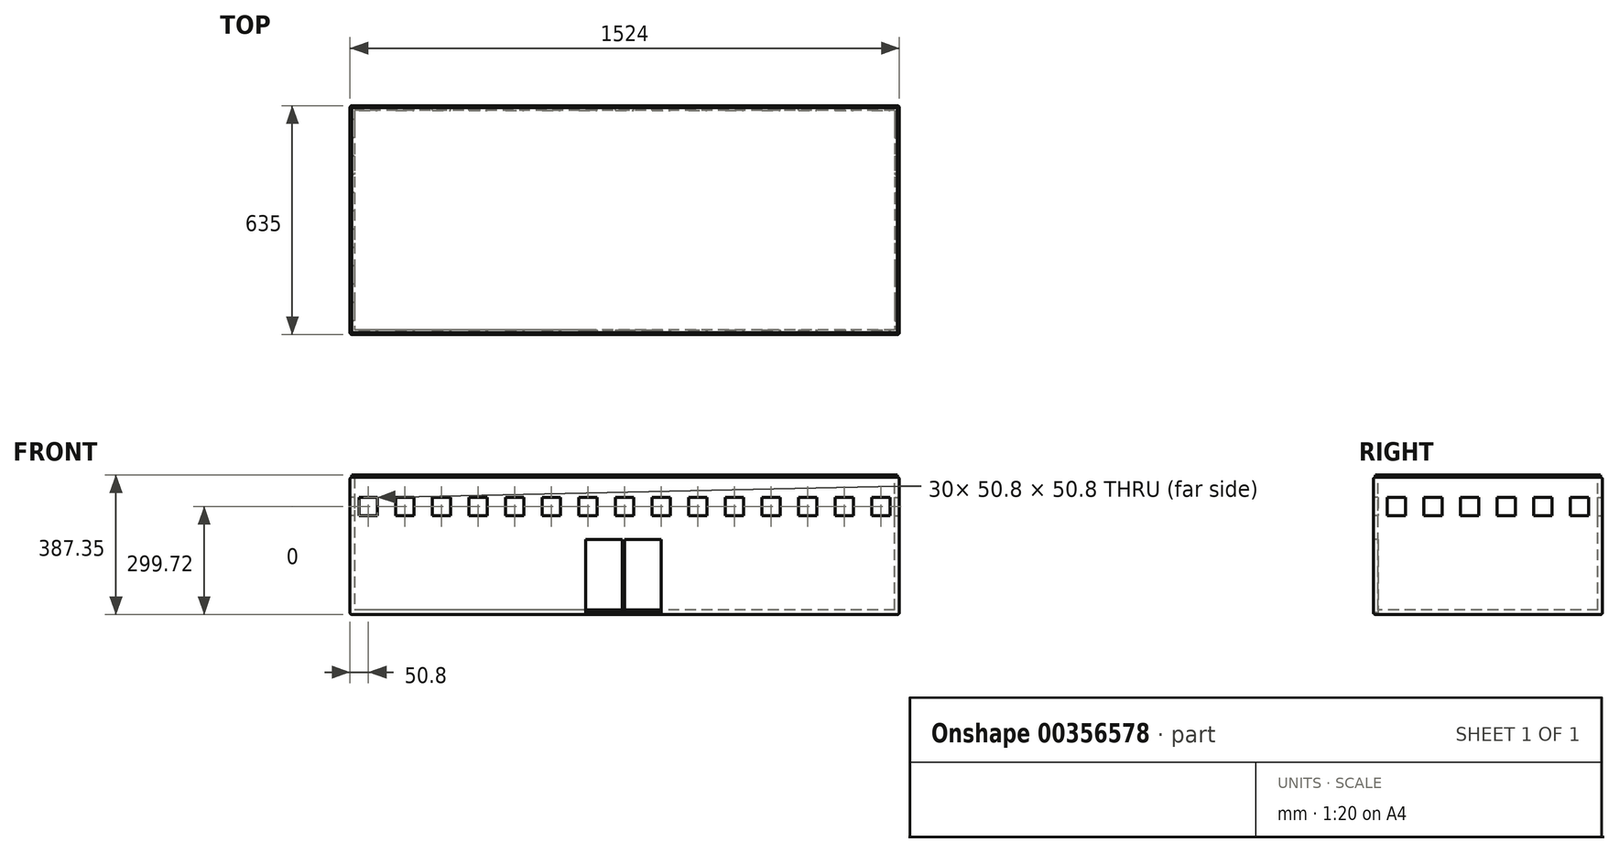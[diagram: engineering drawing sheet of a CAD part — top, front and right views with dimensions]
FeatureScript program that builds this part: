
annotation { "Feature Type Name" : "Feature", "Feature Type Description" : "" }
export const myFeature = defineFeature(function(context is Context, id is Id, definition is map)
    precondition{}
    {
        {
            var Q0;
            Q0=qCreatedBy(makeId("Top.planeOp"),FACE);
            var sketch = newSketch(context, id + "F0", { "sketchPlane" : qUnion([Q0])});
            skLineSegment(sketch, "E0.bottom", {"start": v(-762, 317.5) * mm, "end": v(762, 317.5) * mm});
            skLineSegment(sketch, "E0.top", {"start": v(-762, -317.5) * mm, "end": v(762, -317.5) * mm});
            skLineSegment(sketch, "E0.left", {"start": v(-762, 317.5) * mm, "end": v(-762, -317.5) * mm});
            skLineSegment(sketch, "E0.right", {"start": v(762, 317.5) * mm, "end": v(762, -317.5) * mm});
            skPoint(sketch, "E0.middle", {"position": v(0, 0) * mm});
            skSolve(sketch);
        }
        {
            var Q0;
            Q0 = qSketchRegion(id + "F0", true);
            extrude(context, id + "F1", {"entities" : qUnion([Q0]), "depth" : 381 * mm});
        }
        {
            var Q0;
            Q0=makeQuery(id+"F1.opExtrude","CAP_FACE",FACE,{"disambiguationData":[OSD([sQuery(id+"F0.wireOp",EDGE,"E0.bottom"),sQuery(id+"F0.wireOp",EDGE,"E0.top"),sQuery(id+"F0.wireOp",EDGE,"E0.left"),sQuery(id+"F0.wireOp",EDGE,"E0.right")])],"isStart":false});
            var Q1;
            Q1=makeQuery(id+"F1.opExtrude","SWEPT_FACE",FACE,{"disambiguationData":[OSD([sQuery(id+"F0.wireOp",EDGE,"E0.top")])]});
            var Q2;
            Q2=makeQuery(id+"F1.opExtrude","CAP_FACE",FACE,{"disambiguationData":[OSD([sQuery(id+"F0.wireOp",EDGE,"E0.bottom"),sQuery(id+"F0.wireOp",EDGE,"E0.top"),sQuery(id+"F0.wireOp",EDGE,"E0.left"),sQuery(id+"F0.wireOp",EDGE,"E0.right")])],"isStart":true});
            var Q3;
            Q3=makeQuery(id+"F1.opExtrude","SWEPT_FACE",FACE,{"disambiguationData":[OSD([sQuery(id+"F0.wireOp",EDGE,"E0.bottom")])]});
            fillet(context, id + "F2", {"entities" : qUnion([Q0, Q1, Q2, Q3]), "radius" : 5.08 * mm, "tangentPropagation" : true, "allowEdgeOverflow" : false});
        }
        {
            var Q0;
            Q0=makeQuery(id+"F1.opExtrude","CAP_FACE",FACE,{"disambiguationData":[OSD([sQuery(id+"F0.wireOp",EDGE,"E0.bottom"),sQuery(id+"F0.wireOp",EDGE,"E0.top"),sQuery(id+"F0.wireOp",EDGE,"E0.left"),sQuery(id+"F0.wireOp",EDGE,"E0.right")])],"isStart":false});
            shell(context, id + "F3", {"entities" : qUnion([Q0]), "thickness" : 12.7 * mm});
        }
        {
            var Q0;
            Q0=makeQuery(id+"F1.opExtrude","SWEPT_FACE",FACE,{"disambiguationData":[OSD([sQuery(id+"F0.wireOp",EDGE,"E0.top")])]});
            var sketch = newSketch(context, id + "F4", { "sketchPlane" : qUnion([Q0])});
            skLineSegment(sketch, "E1.bottom", {"start": v(-107.95, 208.28) * mm, "end": v(-6.35, 208.28) * mm});
            skLineSegment(sketch, "E1.top", {"start": v(-107.95, 5.08) * mm, "end": v(-6.35, 5.08) * mm});
            skLineSegment(sketch, "E1.left", {"start": v(-107.95, 208.28) * mm, "end": v(-107.95, 5.08) * mm});
            skLineSegment(sketch, "E1.right", {"start": v(-6.35, 208.28) * mm, "end": v(-6.35, 5.08) * mm});
            skLineSegment(sketch, "E2.bottom", {"start": v(0, 208.28) * mm, "end": v(101.6, 208.28) * mm});
            skLineSegment(sketch, "E2.top", {"start": v(0, 5.08) * mm, "end": v(101.6, 5.08) * mm});
            skLineSegment(sketch, "E2.left", {"start": v(0, 208.28) * mm, "end": v(0, 5.08) * mm});
            skLineSegment(sketch, "E2.right", {"start": v(101.6, 208.28) * mm, "end": v(101.6, 5.08) * mm});
            skSolve(sketch);
        }
        {
            var Q0;
            Q0 = qSketchRegion(id + "F4", true);
            extrude(context, id + "F5", {"entities" : qUnion([Q0]), "operationType" : NewBodyOperationType.REMOVE, "oppositeDirection" : true, "depth" : 12.7 * mm});
        }
        {
            var Q0;
            Q0=makeQuery(id+"F1.opExtrude","SWEPT_FACE",FACE,{"disambiguationData":[OSD([sQuery(id+"F0.wireOp",EDGE,"E0.top")])]});
            var sketch = newSketch(context, id + "F6", { "sketchPlane" : qUnion([Q0])});
            skLineSegment(sketch, "E3.bottom", {"start": v(-685.8, 274.32) * mm, "end": v(-736.6, 274.32) * mm});
            skLineSegment(sketch, "E3.top", {"start": v(-685.8, 325.12) * mm, "end": v(-736.6, 325.12) * mm});
            skLineSegment(sketch, "E3.left", {"start": v(-685.8, 274.32) * mm, "end": v(-685.8, 325.12) * mm});
            skLineSegment(sketch, "E3.right", {"start": v(-736.6, 274.32) * mm, "end": v(-736.6, 325.12) * mm});
            skPoint(sketch, "E3.middle", {"position": v(-711.2, 299.72) * mm});
            skLineSegment(sketch, "E4.1.0.0", {"start": v(-584.2, 274.32) * mm, "end": v(-635, 274.32) * mm});
            skLineSegment(sketch, "E4.1.0.1", {"start": v(-584.2, 325.12) * mm, "end": v(-635, 325.12) * mm});
            skLineSegment(sketch, "E4.1.0.2", {"start": v(-584.2, 274.32) * mm, "end": v(-584.2, 325.12) * mm});
            skLineSegment(sketch, "E4.1.0.3", {"start": v(-635, 274.32) * mm, "end": v(-635, 325.12) * mm});
            skPoint(sketch, "E4.1.0.4", {"position": v(-609.6, 299.72) * mm});
            skLineSegment(sketch, "E4.2.0.0", {"start": v(-482.6, 274.32) * mm, "end": v(-533.4, 274.32) * mm});
            skLineSegment(sketch, "E4.2.0.1", {"start": v(-482.6, 325.12) * mm, "end": v(-533.4, 325.12) * mm});
            skLineSegment(sketch, "E4.2.0.2", {"start": v(-482.6, 274.32) * mm, "end": v(-482.6, 325.12) * mm});
            skLineSegment(sketch, "E4.2.0.3", {"start": v(-533.4, 274.32) * mm, "end": v(-533.4, 325.12) * mm});
            skPoint(sketch, "E4.2.0.4", {"position": v(-508, 299.72) * mm});
            skLineSegment(sketch, "E4.3.0.0", {"start": v(-381, 274.32) * mm, "end": v(-431.8, 274.32) * mm});
            skLineSegment(sketch, "E4.3.0.1", {"start": v(-381, 325.12) * mm, "end": v(-431.8, 325.12) * mm});
            skLineSegment(sketch, "E4.3.0.2", {"start": v(-381, 274.32) * mm, "end": v(-381, 325.12) * mm});
            skLineSegment(sketch, "E4.3.0.3", {"start": v(-431.8, 274.32) * mm, "end": v(-431.8, 325.12) * mm});
            skPoint(sketch, "E4.3.0.4", {"position": v(-406.4, 299.72) * mm});
            skLineSegment(sketch, "E4.4.0.0", {"start": v(-279.4, 274.32) * mm, "end": v(-330.2, 274.32) * mm});
            skLineSegment(sketch, "E4.4.0.1", {"start": v(-279.4, 325.12) * mm, "end": v(-330.2, 325.12) * mm});
            skLineSegment(sketch, "E4.4.0.2", {"start": v(-279.4, 274.32) * mm, "end": v(-279.4, 325.12) * mm});
            skLineSegment(sketch, "E4.4.0.3", {"start": v(-330.2, 274.32) * mm, "end": v(-330.2, 325.12) * mm});
            skPoint(sketch, "E4.4.0.4", {"position": v(-304.8, 299.72) * mm});
            skLineSegment(sketch, "E4.5.0.0", {"start": v(-177.8, 274.32) * mm, "end": v(-228.6, 274.32) * mm});
            skLineSegment(sketch, "E4.5.0.1", {"start": v(-177.8, 325.12) * mm, "end": v(-228.6, 325.12) * mm});
            skLineSegment(sketch, "E4.5.0.2", {"start": v(-177.8, 274.32) * mm, "end": v(-177.8, 325.12) * mm});
            skLineSegment(sketch, "E4.5.0.3", {"start": v(-228.6, 274.32) * mm, "end": v(-228.6, 325.12) * mm});
            skPoint(sketch, "E4.5.0.4", {"position": v(-203.2, 299.72) * mm});
            skLineSegment(sketch, "E4.6.0.0", {"start": v(-76.2, 274.32) * mm, "end": v(-127, 274.32) * mm});
            skLineSegment(sketch, "E4.6.0.1", {"start": v(-76.2, 325.12) * mm, "end": v(-127, 325.12) * mm});
            skLineSegment(sketch, "E4.6.0.2", {"start": v(-76.2, 274.32) * mm, "end": v(-76.2, 325.12) * mm});
            skLineSegment(sketch, "E4.6.0.3", {"start": v(-127, 274.32) * mm, "end": v(-127, 325.12) * mm});
            skPoint(sketch, "E4.6.0.4", {"position": v(-101.6, 299.72) * mm});
            skLineSegment(sketch, "E4.7.0.0", {"start": v(25.4, 274.32) * mm, "end": v(-25.4, 274.32) * mm});
            skLineSegment(sketch, "E4.7.0.1", {"start": v(25.4, 325.12) * mm, "end": v(-25.4, 325.12) * mm});
            skLineSegment(sketch, "E4.7.0.2", {"start": v(25.4, 274.32) * mm, "end": v(25.4, 325.12) * mm});
            skLineSegment(sketch, "E4.7.0.3", {"start": v(-25.4, 274.32) * mm, "end": v(-25.4, 325.12) * mm});
            skPoint(sketch, "E4.7.0.4", {"position": v(0, 299.72) * mm});
            skLineSegment(sketch, "E4.8.0.0", {"start": v(127, 274.32) * mm, "end": v(76.2, 274.32) * mm});
            skLineSegment(sketch, "E4.8.0.1", {"start": v(127, 325.12) * mm, "end": v(76.2, 325.12) * mm});
            skLineSegment(sketch, "E4.8.0.2", {"start": v(127, 274.32) * mm, "end": v(127, 325.12) * mm});
            skLineSegment(sketch, "E4.8.0.3", {"start": v(76.2, 274.32) * mm, "end": v(76.2, 325.12) * mm});
            skPoint(sketch, "E4.8.0.4", {"position": v(101.6, 299.72) * mm});
            skLineSegment(sketch, "E4.9.0.0", {"start": v(228.6, 274.32) * mm, "end": v(177.8, 274.32) * mm});
            skLineSegment(sketch, "E4.9.0.1", {"start": v(228.6, 325.12) * mm, "end": v(177.8, 325.12) * mm});
            skLineSegment(sketch, "E4.9.0.2", {"start": v(228.6, 274.32) * mm, "end": v(228.6, 325.12) * mm});
            skLineSegment(sketch, "E4.9.0.3", {"start": v(177.8, 274.32) * mm, "end": v(177.8, 325.12) * mm});
            skPoint(sketch, "E4.9.0.4", {"position": v(203.2, 299.72) * mm});
            skLineSegment(sketch, "E4.10.0.0", {"start": v(330.2, 274.32) * mm, "end": v(279.4, 274.32) * mm});
            skLineSegment(sketch, "E4.10.0.1", {"start": v(330.2, 325.12) * mm, "end": v(279.4, 325.12) * mm});
            skLineSegment(sketch, "E4.10.0.2", {"start": v(330.2, 274.32) * mm, "end": v(330.2, 325.12) * mm});
            skLineSegment(sketch, "E4.10.0.3", {"start": v(279.4, 274.32) * mm, "end": v(279.4, 325.12) * mm});
            skPoint(sketch, "E4.10.0.4", {"position": v(304.8, 299.72) * mm});
            skLineSegment(sketch, "E4.11.0.0", {"start": v(431.8, 274.32) * mm, "end": v(381, 274.32) * mm});
            skLineSegment(sketch, "E4.11.0.1", {"start": v(431.8, 325.12) * mm, "end": v(381, 325.12) * mm});
            skLineSegment(sketch, "E4.11.0.2", {"start": v(431.8, 274.32) * mm, "end": v(431.8, 325.12) * mm});
            skLineSegment(sketch, "E4.11.0.3", {"start": v(381, 274.32) * mm, "end": v(381, 325.12) * mm});
            skPoint(sketch, "E4.11.0.4", {"position": v(406.4, 299.72) * mm});
            skLineSegment(sketch, "E4.12.0.0", {"start": v(533.4, 274.32) * mm, "end": v(482.6, 274.32) * mm});
            skLineSegment(sketch, "E4.12.0.1", {"start": v(533.4, 325.12) * mm, "end": v(482.6, 325.12) * mm});
            skLineSegment(sketch, "E4.12.0.2", {"start": v(533.4, 274.32) * mm, "end": v(533.4, 325.12) * mm});
            skLineSegment(sketch, "E4.12.0.3", {"start": v(482.6, 274.32) * mm, "end": v(482.6, 325.12) * mm});
            skPoint(sketch, "E4.12.0.4", {"position": v(508, 299.72) * mm});
            skLineSegment(sketch, "E4.13.0.0", {"start": v(635, 274.32) * mm, "end": v(584.2, 274.32) * mm});
            skLineSegment(sketch, "E4.13.0.1", {"start": v(635, 325.12) * mm, "end": v(584.2, 325.12) * mm});
            skLineSegment(sketch, "E4.13.0.2", {"start": v(635, 274.32) * mm, "end": v(635, 325.12) * mm});
            skLineSegment(sketch, "E4.13.0.3", {"start": v(584.2, 274.32) * mm, "end": v(584.2, 325.12) * mm});
            skPoint(sketch, "E4.13.0.4", {"position": v(609.6, 299.72) * mm});
            skLineSegment(sketch, "E4.14.0.0", {"start": v(736.6, 274.32) * mm, "end": v(685.8, 274.32) * mm});
            skLineSegment(sketch, "E4.14.0.1", {"start": v(736.6, 325.12) * mm, "end": v(685.8, 325.12) * mm});
            skLineSegment(sketch, "E4.14.0.2", {"start": v(736.6, 274.32) * mm, "end": v(736.6, 325.12) * mm});
            skLineSegment(sketch, "E4.14.0.3", {"start": v(685.8, 274.32) * mm, "end": v(685.8, 325.12) * mm});
            skPoint(sketch, "E4.14.0.4", {"position": v(711.2, 299.72) * mm});
            skLineSegment(sketch, "E4.direction1", {"start": v(-736.6, 274.32) * mm, "end": v(-635, 274.32) * mm, "construction": true});
            skSolve(sketch);
        }
        {
            var Q0;
            Q0=makeQuery(id+"F6.imprint","IMPRINT",FACE,{"disambiguationData":[TD([[makeQuery(id+"F6.imprint","IMPRINT",EDGE,{"derivedFrom":sQuery(id+"F6.wireOp",EDGE,"E4.1.0.0")}),-1.0]])]});
            var Q1;
            Q1=makeQuery(id+"F6.imprint","IMPRINT",FACE,{"disambiguationData":[TD([[makeQuery(id+"F6.imprint","IMPRINT",EDGE,{"derivedFrom":sQuery(id+"F6.wireOp",EDGE,"E4.14.0.0")}),-1.0]])]});
            var Q2;
            Q2=makeQuery(id+"F6.imprint","IMPRINT",FACE,{"disambiguationData":[TD([[makeQuery(id+"F6.imprint","IMPRINT",EDGE,{"derivedFrom":sQuery(id+"F6.wireOp",EDGE,"E4.5.0.0")}),-1.0]])]});
            var Q3;
            Q3=makeQuery(id+"F6.imprint","IMPRINT",FACE,{"disambiguationData":[TD([[makeQuery(id+"F6.imprint","IMPRINT",EDGE,{"derivedFrom":sQuery(id+"F6.wireOp",EDGE,"E4.3.0.0")}),-1.0]])]});
            var Q4;
            Q4=makeQuery(id+"F6.imprint","IMPRINT",FACE,{"disambiguationData":[TD([[makeQuery(id+"F6.imprint","IMPRINT",EDGE,{"derivedFrom":sQuery(id+"F6.wireOp",EDGE,"E4.2.0.0")}),-1.0]])]});
            var Q5;
            Q5=makeQuery(id+"F6.imprint","IMPRINT",FACE,{"disambiguationData":[TD([[makeQuery(id+"F6.imprint","IMPRINT",EDGE,{"derivedFrom":sQuery(id+"F6.wireOp",EDGE,"E4.4.0.0")}),-1.0]])]});
            var Q6;
            Q6=makeQuery(id+"F6.imprint","IMPRINT",FACE,{"disambiguationData":[TD([[makeQuery(id+"F6.imprint","IMPRINT",EDGE,{"derivedFrom":sQuery(id+"F6.wireOp",EDGE,"E4.11.0.0")}),-1.0]])]});
            var Q7;
            Q7=makeQuery(id+"F6.imprint","IMPRINT",FACE,{"disambiguationData":[TD([[makeQuery(id+"F6.imprint","IMPRINT",EDGE,{"derivedFrom":sQuery(id+"F6.wireOp",EDGE,"E4.10.0.0")}),-1.0]])]});
            var Q8;
            Q8=makeQuery(id+"F6.imprint","IMPRINT",FACE,{"disambiguationData":[TD([[makeQuery(id+"F6.imprint","IMPRINT",EDGE,{"derivedFrom":sQuery(id+"F6.wireOp",EDGE,"E4.8.0.0")}),-1.0]])]});
            var Q9;
            Q9=makeQuery(id+"F6.imprint","IMPRINT",FACE,{"disambiguationData":[TD([[makeQuery(id+"F6.imprint","IMPRINT",EDGE,{"derivedFrom":sQuery(id+"F6.wireOp",EDGE,"E4.9.0.0")}),-1.0]])]});
            var Q10;
            Q10=makeQuery(id+"F6.imprint","IMPRINT",FACE,{"disambiguationData":[TD([[makeQuery(id+"F6.imprint","IMPRINT",EDGE,{"derivedFrom":sQuery(id+"F6.wireOp",EDGE,"E4.7.0.0")}),-1.0]])]});
            var Q11;
            Q11=makeQuery(id+"F6.imprint","IMPRINT",FACE,{"disambiguationData":[TD([[makeQuery(id+"F6.imprint","IMPRINT",EDGE,{"derivedFrom":sQuery(id+"F6.wireOp",EDGE,"E4.6.0.0")}),-1.0]])]});
            var Q12;
            Q12=makeQuery(id+"F6.imprint","IMPRINT",FACE,{"disambiguationData":[TD([[makeQuery(id+"F6.imprint","IMPRINT",EDGE,{"derivedFrom":sQuery(id+"F6.wireOp",EDGE,"E4.12.0.0")}),-1.0]])]});
            var Q13;
            Q13=makeQuery(id+"F6.imprint","IMPRINT",FACE,{"disambiguationData":[TD([[makeQuery(id+"F6.imprint","IMPRINT",EDGE,{"derivedFrom":sQuery(id+"F6.wireOp",EDGE,"E4.13.0.0")}),-1.0]])]});
            var Q14;
            Q14=makeQuery(id+"F6.imprint","IMPRINT",FACE,{"disambiguationData":[TD([[makeQuery(id+"F6.imprint","IMPRINT",EDGE,{"derivedFrom":sQuery(id+"F6.wireOp",EDGE,"E3.bottom")}),-1.0]])]});
            extrude(context, id + "F7", {"entities" : qUnion([Q0, Q1, Q2, Q3, Q4, Q5, Q6, Q7, Q8, Q9, Q10, Q11, Q12, Q13, Q14]), "operationType" : NewBodyOperationType.REMOVE, "oppositeDirection" : true, "depth" : 25.4 * mm});
        }
        {
            var Q0;
            Q0=makeQuery(id+"F1.opExtrude","SWEPT_FACE",FACE,{"disambiguationData":[OSD([sQuery(id+"F0.wireOp",EDGE,"E0.left")])]});
            var sketch = newSketch(context, id + "F8", { "sketchPlane" : qUnion([Q0])});
            skLineSegment(sketch, "E5.bottom", {"start": v(-228.6, 274.32) * mm, "end": v(-279.4, 274.32) * mm});
            skLineSegment(sketch, "E5.top", {"start": v(-228.6, 325.12) * mm, "end": v(-279.4, 325.12) * mm});
            skLineSegment(sketch, "E5.left", {"start": v(-228.6, 274.32) * mm, "end": v(-228.6, 325.12) * mm});
            skLineSegment(sketch, "E5.right", {"start": v(-279.4, 274.32) * mm, "end": v(-279.4, 325.12) * mm});
            skPoint(sketch, "E5.middle", {"position": v(-254, 299.72) * mm});
            skLineSegment(sketch, "E6.1.0.0", {"start": v(-127, 274.32) * mm, "end": v(-177.8, 274.32) * mm});
            skLineSegment(sketch, "E6.1.0.1", {"start": v(-127, 325.12) * mm, "end": v(-177.8, 325.12) * mm});
            skLineSegment(sketch, "E6.1.0.2", {"start": v(-127, 274.32) * mm, "end": v(-127, 325.12) * mm});
            skLineSegment(sketch, "E6.1.0.3", {"start": v(-177.8, 274.32) * mm, "end": v(-177.8, 325.12) * mm});
            skPoint(sketch, "E6.1.0.4", {"position": v(-152.4, 299.72) * mm});
            skLineSegment(sketch, "E6.2.0.0", {"start": v(-25.4, 274.32) * mm, "end": v(-76.2, 274.32) * mm});
            skLineSegment(sketch, "E6.2.0.1", {"start": v(-25.4, 325.12) * mm, "end": v(-76.2, 325.12) * mm});
            skLineSegment(sketch, "E6.2.0.2", {"start": v(-25.4, 274.32) * mm, "end": v(-25.4, 325.12) * mm});
            skLineSegment(sketch, "E6.2.0.3", {"start": v(-76.2, 274.32) * mm, "end": v(-76.2, 325.12) * mm});
            skPoint(sketch, "E6.2.0.4", {"position": v(-50.8, 299.72) * mm});
            skLineSegment(sketch, "E6.3.0.0", {"start": v(76.2, 274.32) * mm, "end": v(25.4, 274.32) * mm});
            skLineSegment(sketch, "E6.3.0.1", {"start": v(76.2, 325.12) * mm, "end": v(25.4, 325.12) * mm});
            skLineSegment(sketch, "E6.3.0.2", {"start": v(76.2, 274.32) * mm, "end": v(76.2, 325.12) * mm});
            skLineSegment(sketch, "E6.3.0.3", {"start": v(25.4, 274.32) * mm, "end": v(25.4, 325.12) * mm});
            skPoint(sketch, "E6.3.0.4", {"position": v(50.8, 299.72) * mm});
            skLineSegment(sketch, "E6.4.0.0", {"start": v(177.8, 274.32) * mm, "end": v(127, 274.32) * mm});
            skLineSegment(sketch, "E6.4.0.1", {"start": v(177.8, 325.12) * mm, "end": v(127, 325.12) * mm});
            skLineSegment(sketch, "E6.4.0.2", {"start": v(177.8, 274.32) * mm, "end": v(177.8, 325.12) * mm});
            skLineSegment(sketch, "E6.4.0.3", {"start": v(127, 274.32) * mm, "end": v(127, 325.12) * mm});
            skPoint(sketch, "E6.4.0.4", {"position": v(152.4, 299.72) * mm});
            skLineSegment(sketch, "E6.5.0.0", {"start": v(279.4, 274.32) * mm, "end": v(228.6, 274.32) * mm});
            skLineSegment(sketch, "E6.5.0.1", {"start": v(279.4, 325.12) * mm, "end": v(228.6, 325.12) * mm});
            skLineSegment(sketch, "E6.5.0.2", {"start": v(279.4, 274.32) * mm, "end": v(279.4, 325.12) * mm});
            skLineSegment(sketch, "E6.5.0.3", {"start": v(228.6, 274.32) * mm, "end": v(228.6, 325.12) * mm});
            skPoint(sketch, "E6.5.0.4", {"position": v(254, 299.72) * mm});
            skLineSegment(sketch, "E6.direction1", {"start": v(-279.4, 274.32) * mm, "end": v(-177.8, 274.32) * mm, "construction": true});
            skSolve(sketch);
        }
        {
            var Q0;
            Q0=makeQuery(id+"F8.imprint","IMPRINT",FACE,{"disambiguationData":[TD([[makeQuery(id+"F8.imprint","IMPRINT",EDGE,{"derivedFrom":sQuery(id+"F8.wireOp",EDGE,"E6.5.0.0")}),-1.0]])]});
            var Q1;
            Q1=makeQuery(id+"F8.imprint","IMPRINT",FACE,{"disambiguationData":[TD([[makeQuery(id+"F8.imprint","IMPRINT",EDGE,{"derivedFrom":sQuery(id+"F8.wireOp",EDGE,"E6.4.0.0")}),-1.0]])]});
            var Q2;
            Q2=makeQuery(id+"F8.imprint","IMPRINT",FACE,{"disambiguationData":[TD([[makeQuery(id+"F8.imprint","IMPRINT",EDGE,{"derivedFrom":sQuery(id+"F8.wireOp",EDGE,"E6.3.0.0")}),-1.0]])]});
            var Q3;
            Q3=makeQuery(id+"F8.imprint","IMPRINT",FACE,{"disambiguationData":[TD([[makeQuery(id+"F8.imprint","IMPRINT",EDGE,{"derivedFrom":sQuery(id+"F8.wireOp",EDGE,"E6.2.0.0")}),-1.0]])]});
            var Q4;
            Q4=makeQuery(id+"F8.imprint","IMPRINT",FACE,{"disambiguationData":[TD([[makeQuery(id+"F8.imprint","IMPRINT",EDGE,{"derivedFrom":sQuery(id+"F8.wireOp",EDGE,"E6.1.0.0")}),-1.0]])]});
            var Q5;
            Q5=makeQuery(id+"F8.imprint","IMPRINT",FACE,{"disambiguationData":[TD([[makeQuery(id+"F8.imprint","IMPRINT",EDGE,{"derivedFrom":sQuery(id+"F8.wireOp",EDGE,"E5.bottom")}),-1.0]])]});
            extrude(context, id + "F9", {"entities" : qUnion([Q0, Q1, Q2, Q3, Q4, Q5]), "operationType" : NewBodyOperationType.REMOVE, "oppositeDirection" : true, "depth" : 25.4 * mm});
        }
        {
            var Q0;
            Q0=makeQuery(id+"F1.opExtrude","SWEPT_FACE",FACE,{"disambiguationData":[OSD([sQuery(id+"F0.wireOp",EDGE,"E0.bottom")])]});
            var sketch = newSketch(context, id + "F10", { "sketchPlane" : qUnion([Q0])});
            skLineSegment(sketch, "E7.bottom", {"start": v(-685.8, 274.32) * mm, "end": v(-736.6, 274.32) * mm});
            skLineSegment(sketch, "E7.top", {"start": v(-685.8, 325.12) * mm, "end": v(-736.6, 325.12) * mm});
            skLineSegment(sketch, "E7.left", {"start": v(-685.8, 274.32) * mm, "end": v(-685.8, 325.12) * mm});
            skLineSegment(sketch, "E7.right", {"start": v(-736.6, 274.32) * mm, "end": v(-736.6, 325.12) * mm});
            skPoint(sketch, "E7.middle", {"position": v(-711.2, 299.72) * mm});
            skPoint(sketch, "E8.1.0.0", {"position": v(-609.6, 299.72) * mm});
            skLineSegment(sketch, "E8.1.0.1", {"start": v(-635, 274.32) * mm, "end": v(-635, 325.12) * mm});
            skLineSegment(sketch, "E8.1.0.2", {"start": v(-584.2, 274.32) * mm, "end": v(-584.2, 325.12) * mm});
            skLineSegment(sketch, "E8.1.0.3", {"start": v(-584.2, 325.12) * mm, "end": v(-635, 325.12) * mm});
            skLineSegment(sketch, "E8.1.0.4", {"start": v(-584.2, 274.32) * mm, "end": v(-635, 274.32) * mm});
            skPoint(sketch, "E8.2.0.0", {"position": v(-508, 299.72) * mm});
            skLineSegment(sketch, "E8.2.0.1", {"start": v(-533.4, 274.32) * mm, "end": v(-533.4, 325.12) * mm});
            skLineSegment(sketch, "E8.2.0.2", {"start": v(-482.6, 274.32) * mm, "end": v(-482.6, 325.12) * mm});
            skLineSegment(sketch, "E8.2.0.3", {"start": v(-482.6, 325.12) * mm, "end": v(-533.4, 325.12) * mm});
            skLineSegment(sketch, "E8.2.0.4", {"start": v(-482.6, 274.32) * mm, "end": v(-533.4, 274.32) * mm});
            skPoint(sketch, "E8.3.0.0", {"position": v(-406.4, 299.72) * mm});
            skLineSegment(sketch, "E8.3.0.1", {"start": v(-431.8, 274.32) * mm, "end": v(-431.8, 325.12) * mm});
            skLineSegment(sketch, "E8.3.0.2", {"start": v(-381, 274.32) * mm, "end": v(-381, 325.12) * mm});
            skLineSegment(sketch, "E8.3.0.3", {"start": v(-381, 325.12) * mm, "end": v(-431.8, 325.12) * mm});
            skLineSegment(sketch, "E8.3.0.4", {"start": v(-381, 274.32) * mm, "end": v(-431.8, 274.32) * mm});
            skPoint(sketch, "E8.4.0.0", {"position": v(-304.8, 299.72) * mm});
            skLineSegment(sketch, "E8.4.0.1", {"start": v(-330.2, 274.32) * mm, "end": v(-330.2, 325.12) * mm});
            skLineSegment(sketch, "E8.4.0.2", {"start": v(-279.4, 274.32) * mm, "end": v(-279.4, 325.12) * mm});
            skLineSegment(sketch, "E8.4.0.3", {"start": v(-279.4, 325.12) * mm, "end": v(-330.2, 325.12) * mm});
            skLineSegment(sketch, "E8.4.0.4", {"start": v(-279.4, 274.32) * mm, "end": v(-330.2, 274.32) * mm});
            skPoint(sketch, "E8.5.0.0", {"position": v(-203.2, 299.72) * mm});
            skLineSegment(sketch, "E8.5.0.1", {"start": v(-228.6, 274.32) * mm, "end": v(-228.6, 325.12) * mm});
            skLineSegment(sketch, "E8.5.0.2", {"start": v(-177.8, 274.32) * mm, "end": v(-177.8, 325.12) * mm});
            skLineSegment(sketch, "E8.5.0.3", {"start": v(-177.8, 325.12) * mm, "end": v(-228.6, 325.12) * mm});
            skLineSegment(sketch, "E8.5.0.4", {"start": v(-177.8, 274.32) * mm, "end": v(-228.6, 274.32) * mm});
            skPoint(sketch, "E8.6.0.0", {"position": v(-101.6, 299.72) * mm});
            skLineSegment(sketch, "E8.6.0.1", {"start": v(-127, 274.32) * mm, "end": v(-127, 325.12) * mm});
            skLineSegment(sketch, "E8.6.0.2", {"start": v(-76.2, 274.32) * mm, "end": v(-76.2, 325.12) * mm});
            skLineSegment(sketch, "E8.6.0.3", {"start": v(-76.2, 325.12) * mm, "end": v(-127, 325.12) * mm});
            skLineSegment(sketch, "E8.6.0.4", {"start": v(-76.2, 274.32) * mm, "end": v(-127, 274.32) * mm});
            skPoint(sketch, "E8.7.0.0", {"position": v(0, 299.72) * mm});
            skLineSegment(sketch, "E8.7.0.1", {"start": v(-25.4, 274.32) * mm, "end": v(-25.4, 325.12) * mm});
            skLineSegment(sketch, "E8.7.0.2", {"start": v(25.4, 274.32) * mm, "end": v(25.4, 325.12) * mm});
            skLineSegment(sketch, "E8.7.0.3", {"start": v(25.4, 325.12) * mm, "end": v(-25.4, 325.12) * mm});
            skLineSegment(sketch, "E8.7.0.4", {"start": v(25.4, 274.32) * mm, "end": v(-25.4, 274.32) * mm});
            skPoint(sketch, "E8.8.0.0", {"position": v(101.6, 299.72) * mm});
            skLineSegment(sketch, "E8.8.0.1", {"start": v(76.2, 274.32) * mm, "end": v(76.2, 325.12) * mm});
            skLineSegment(sketch, "E8.8.0.2", {"start": v(127, 274.32) * mm, "end": v(127, 325.12) * mm});
            skLineSegment(sketch, "E8.8.0.3", {"start": v(127, 325.12) * mm, "end": v(76.2, 325.12) * mm});
            skLineSegment(sketch, "E8.8.0.4", {"start": v(127, 274.32) * mm, "end": v(76.2, 274.32) * mm});
            skPoint(sketch, "E8.9.0.0", {"position": v(203.2, 299.72) * mm});
            skLineSegment(sketch, "E8.9.0.1", {"start": v(177.8, 274.32) * mm, "end": v(177.8, 325.12) * mm});
            skLineSegment(sketch, "E8.9.0.2", {"start": v(228.6, 274.32) * mm, "end": v(228.6, 325.12) * mm});
            skLineSegment(sketch, "E8.9.0.3", {"start": v(228.6, 325.12) * mm, "end": v(177.8, 325.12) * mm});
            skLineSegment(sketch, "E8.9.0.4", {"start": v(228.6, 274.32) * mm, "end": v(177.8, 274.32) * mm});
            skPoint(sketch, "E8.10.0.0", {"position": v(304.8, 299.72) * mm});
            skLineSegment(sketch, "E8.10.0.1", {"start": v(279.4, 274.32) * mm, "end": v(279.4, 325.12) * mm});
            skLineSegment(sketch, "E8.10.0.2", {"start": v(330.2, 274.32) * mm, "end": v(330.2, 325.12) * mm});
            skLineSegment(sketch, "E8.10.0.3", {"start": v(330.2, 325.12) * mm, "end": v(279.4, 325.12) * mm});
            skLineSegment(sketch, "E8.10.0.4", {"start": v(330.2, 274.32) * mm, "end": v(279.4, 274.32) * mm});
            skPoint(sketch, "E8.11.0.0", {"position": v(406.4, 299.72) * mm});
            skLineSegment(sketch, "E8.11.0.1", {"start": v(381, 274.32) * mm, "end": v(381, 325.12) * mm});
            skLineSegment(sketch, "E8.11.0.2", {"start": v(431.8, 274.32) * mm, "end": v(431.8, 325.12) * mm});
            skLineSegment(sketch, "E8.11.0.3", {"start": v(431.8, 325.12) * mm, "end": v(381, 325.12) * mm});
            skLineSegment(sketch, "E8.11.0.4", {"start": v(431.8, 274.32) * mm, "end": v(381, 274.32) * mm});
            skPoint(sketch, "E8.12.0.0", {"position": v(508, 299.72) * mm});
            skLineSegment(sketch, "E8.12.0.1", {"start": v(482.6, 274.32) * mm, "end": v(482.6, 325.12) * mm});
            skLineSegment(sketch, "E8.12.0.2", {"start": v(533.4, 274.32) * mm, "end": v(533.4, 325.12) * mm});
            skLineSegment(sketch, "E8.12.0.3", {"start": v(533.4, 325.12) * mm, "end": v(482.6, 325.12) * mm});
            skLineSegment(sketch, "E8.12.0.4", {"start": v(533.4, 274.32) * mm, "end": v(482.6, 274.32) * mm});
            skPoint(sketch, "E8.13.0.0", {"position": v(609.6, 299.72) * mm});
            skLineSegment(sketch, "E8.13.0.1", {"start": v(584.2, 274.32) * mm, "end": v(584.2, 325.12) * mm});
            skLineSegment(sketch, "E8.13.0.2", {"start": v(635, 274.32) * mm, "end": v(635, 325.12) * mm});
            skLineSegment(sketch, "E8.13.0.3", {"start": v(635, 325.12) * mm, "end": v(584.2, 325.12) * mm});
            skLineSegment(sketch, "E8.13.0.4", {"start": v(635, 274.32) * mm, "end": v(584.2, 274.32) * mm});
            skPoint(sketch, "E8.14.0.0", {"position": v(711.2, 299.72) * mm});
            skLineSegment(sketch, "E8.14.0.1", {"start": v(685.8, 274.32) * mm, "end": v(685.8, 325.12) * mm});
            skLineSegment(sketch, "E8.14.0.2", {"start": v(736.6, 274.32) * mm, "end": v(736.6, 325.12) * mm});
            skLineSegment(sketch, "E8.14.0.3", {"start": v(736.6, 325.12) * mm, "end": v(685.8, 325.12) * mm});
            skLineSegment(sketch, "E8.14.0.4", {"start": v(736.6, 274.32) * mm, "end": v(685.8, 274.32) * mm});
            skLineSegment(sketch, "E8.direction1", {"start": v(-736.6, 274.32) * mm, "end": v(-635, 274.32) * mm, "construction": true});
            skSolve(sketch);
        }
        {
            var Q0;
            Q0=makeQuery(id+"F10.imprint","IMPRINT",FACE,{"disambiguationData":[TD([[makeQuery(id+"F10.imprint","IMPRINT",EDGE,{"derivedFrom":sQuery(id+"F10.wireOp",EDGE,"E8.13.0.1")}),-1.0]])]});
            var Q1;
            Q1=makeQuery(id+"F10.imprint","IMPRINT",FACE,{"disambiguationData":[TD([[makeQuery(id+"F10.imprint","IMPRINT",EDGE,{"derivedFrom":sQuery(id+"F10.wireOp",EDGE,"E8.14.0.1")}),-1.0]])]});
            var Q2;
            Q2=makeQuery(id+"F10.imprint","IMPRINT",FACE,{"disambiguationData":[TD([[makeQuery(id+"F10.imprint","IMPRINT",EDGE,{"derivedFrom":sQuery(id+"F10.wireOp",EDGE,"E7.bottom")}),-1.0]])]});
            var Q3;
            Q3=makeQuery(id+"F10.imprint","IMPRINT",FACE,{"disambiguationData":[TD([[makeQuery(id+"F10.imprint","IMPRINT",EDGE,{"derivedFrom":sQuery(id+"F10.wireOp",EDGE,"E8.1.0.1")}),-1.0]])]});
            var Q4;
            Q4=makeQuery(id+"F10.imprint","IMPRINT",FACE,{"disambiguationData":[TD([[makeQuery(id+"F10.imprint","IMPRINT",EDGE,{"derivedFrom":sQuery(id+"F10.wireOp",EDGE,"E8.2.0.1")}),-1.0]])]});
            var Q5;
            Q5=makeQuery(id+"F10.imprint","IMPRINT",FACE,{"disambiguationData":[TD([[makeQuery(id+"F10.imprint","IMPRINT",EDGE,{"derivedFrom":sQuery(id+"F10.wireOp",EDGE,"E8.3.0.1")}),-1.0]])]});
            var Q6;
            Q6=makeQuery(id+"F10.imprint","IMPRINT",FACE,{"disambiguationData":[TD([[makeQuery(id+"F10.imprint","IMPRINT",EDGE,{"derivedFrom":sQuery(id+"F10.wireOp",EDGE,"E8.4.0.1")}),-1.0]])]});
            var Q7;
            Q7=makeQuery(id+"F10.imprint","IMPRINT",FACE,{"disambiguationData":[TD([[makeQuery(id+"F10.imprint","IMPRINT",EDGE,{"derivedFrom":sQuery(id+"F10.wireOp",EDGE,"E8.5.0.1")}),-1.0]])]});
            var Q8;
            Q8=makeQuery(id+"F10.imprint","IMPRINT",FACE,{"disambiguationData":[TD([[makeQuery(id+"F10.imprint","IMPRINT",EDGE,{"derivedFrom":sQuery(id+"F10.wireOp",EDGE,"E8.6.0.1")}),-1.0]])]});
            var Q9;
            Q9=makeQuery(id+"F10.imprint","IMPRINT",FACE,{"disambiguationData":[TD([[makeQuery(id+"F10.imprint","IMPRINT",EDGE,{"derivedFrom":sQuery(id+"F10.wireOp",EDGE,"E8.7.0.1")}),-1.0]])]});
            var Q10;
            Q10=makeQuery(id+"F10.imprint","IMPRINT",FACE,{"disambiguationData":[TD([[makeQuery(id+"F10.imprint","IMPRINT",EDGE,{"derivedFrom":sQuery(id+"F10.wireOp",EDGE,"E8.8.0.1")}),-1.0]])]});
            var Q11;
            Q11=makeQuery(id+"F10.imprint","IMPRINT",FACE,{"disambiguationData":[TD([[makeQuery(id+"F10.imprint","IMPRINT",EDGE,{"derivedFrom":sQuery(id+"F10.wireOp",EDGE,"E8.9.0.1")}),-1.0]])]});
            var Q12;
            Q12=makeQuery(id+"F10.imprint","IMPRINT",FACE,{"disambiguationData":[TD([[makeQuery(id+"F10.imprint","IMPRINT",EDGE,{"derivedFrom":sQuery(id+"F10.wireOp",EDGE,"E8.10.0.1")}),-1.0]])]});
            var Q13;
            Q13=makeQuery(id+"F10.imprint","IMPRINT",FACE,{"disambiguationData":[TD([[makeQuery(id+"F10.imprint","IMPRINT",EDGE,{"derivedFrom":sQuery(id+"F10.wireOp",EDGE,"E8.11.0.1")}),-1.0]])]});
            var Q14;
            Q14=makeQuery(id+"F10.imprint","IMPRINT",FACE,{"disambiguationData":[TD([[makeQuery(id+"F10.imprint","IMPRINT",EDGE,{"derivedFrom":sQuery(id+"F10.wireOp",EDGE,"E8.12.0.1")}),-1.0]])]});
            extrude(context, id + "F11", {"entities" : qUnion([Q0, Q1, Q2, Q3, Q4, Q5, Q6, Q7, Q8, Q9, Q10, Q11, Q12, Q13, Q14]), "operationType" : NewBodyOperationType.REMOVE, "oppositeDirection" : true, "depth" : 25.4 * mm});
        }
        {
            var Q0;
            Q0=makeQuery(id+"F1.opExtrude","SWEPT_FACE",FACE,{"disambiguationData":[OSD([sQuery(id+"F0.wireOp",EDGE,"E0.right")])]});
            var sketch = newSketch(context, id + "F12", { "sketchPlane" : qUnion([Q0])});
            skLineSegment(sketch, "E9.bottom", {"start": v(-228.6, 274.32) * mm, "end": v(-279.4, 274.32) * mm});
            skLineSegment(sketch, "E9.top", {"start": v(-228.6, 325.12) * mm, "end": v(-279.4, 325.12) * mm});
            skLineSegment(sketch, "E9.left", {"start": v(-228.6, 274.32) * mm, "end": v(-228.6, 325.12) * mm});
            skLineSegment(sketch, "E9.right", {"start": v(-279.4, 274.32) * mm, "end": v(-279.4, 325.12) * mm});
            skPoint(sketch, "E9.middle", {"position": v(-254, 299.72) * mm});
            skLineSegment(sketch, "E10.1.0.0", {"start": v(-127, 274.32) * mm, "end": v(-127, 325.12) * mm});
            skLineSegment(sketch, "E10.1.0.1", {"start": v(-177.8, 274.32) * mm, "end": v(-177.8, 325.12) * mm});
            skLineSegment(sketch, "E10.1.0.2", {"start": v(-127, 325.12) * mm, "end": v(-177.8, 325.12) * mm});
            skPoint(sketch, "E10.1.0.3", {"position": v(-152.4, 299.72) * mm});
            skLineSegment(sketch, "E10.1.0.4", {"start": v(-127, 274.32) * mm, "end": v(-177.8, 274.32) * mm});
            skLineSegment(sketch, "E10.2.0.0", {"start": v(-25.4, 274.32) * mm, "end": v(-25.4, 325.12) * mm});
            skLineSegment(sketch, "E10.2.0.1", {"start": v(-76.2, 274.32) * mm, "end": v(-76.2, 325.12) * mm});
            skLineSegment(sketch, "E10.2.0.2", {"start": v(-25.4, 325.12) * mm, "end": v(-76.2, 325.12) * mm});
            skPoint(sketch, "E10.2.0.3", {"position": v(-50.8, 299.72) * mm});
            skLineSegment(sketch, "E10.2.0.4", {"start": v(-25.4, 274.32) * mm, "end": v(-76.2, 274.32) * mm});
            skLineSegment(sketch, "E10.3.0.0", {"start": v(76.2, 274.32) * mm, "end": v(76.2, 325.12) * mm});
            skLineSegment(sketch, "E10.3.0.1", {"start": v(25.4, 274.32) * mm, "end": v(25.4, 325.12) * mm});
            skLineSegment(sketch, "E10.3.0.2", {"start": v(76.2, 325.12) * mm, "end": v(25.4, 325.12) * mm});
            skPoint(sketch, "E10.3.0.3", {"position": v(50.8, 299.72) * mm});
            skLineSegment(sketch, "E10.3.0.4", {"start": v(76.2, 274.32) * mm, "end": v(25.4, 274.32) * mm});
            skLineSegment(sketch, "E10.4.0.0", {"start": v(177.8, 274.32) * mm, "end": v(177.8, 325.12) * mm});
            skLineSegment(sketch, "E10.4.0.1", {"start": v(127, 274.32) * mm, "end": v(127, 325.12) * mm});
            skLineSegment(sketch, "E10.4.0.2", {"start": v(177.8, 325.12) * mm, "end": v(127, 325.12) * mm});
            skPoint(sketch, "E10.4.0.3", {"position": v(152.4, 299.72) * mm});
            skLineSegment(sketch, "E10.4.0.4", {"start": v(177.8, 274.32) * mm, "end": v(127, 274.32) * mm});
            skLineSegment(sketch, "E10.5.0.0", {"start": v(279.4, 274.32) * mm, "end": v(279.4, 325.12) * mm});
            skLineSegment(sketch, "E10.5.0.1", {"start": v(228.6, 274.32) * mm, "end": v(228.6, 325.12) * mm});
            skLineSegment(sketch, "E10.5.0.2", {"start": v(279.4, 325.12) * mm, "end": v(228.6, 325.12) * mm});
            skPoint(sketch, "E10.5.0.3", {"position": v(254, 299.72) * mm});
            skLineSegment(sketch, "E10.5.0.4", {"start": v(279.4, 274.32) * mm, "end": v(228.6, 274.32) * mm});
            skLineSegment(sketch, "E10.direction1", {"start": v(-279.4, 274.32) * mm, "end": v(-177.8, 274.32) * mm, "construction": true});
            skSolve(sketch);
        }
        {
            var Q0;
            Q0=makeQuery(id+"F12.imprint","IMPRINT",FACE,{"disambiguationData":[TD([[makeQuery(id+"F12.imprint","IMPRINT",EDGE,{"derivedFrom":sQuery(id+"F12.wireOp",EDGE,"E9.bottom")}),-1.0]])]});
            var Q1;
            Q1=makeQuery(id+"F12.imprint","IMPRINT",FACE,{"disambiguationData":[TD([[makeQuery(id+"F12.imprint","IMPRINT",EDGE,{"derivedFrom":sQuery(id+"F12.wireOp",EDGE,"E10.1.0.0")}),1.0]])]});
            var Q2;
            Q2=makeQuery(id+"F12.imprint","IMPRINT",FACE,{"disambiguationData":[TD([[makeQuery(id+"F12.imprint","IMPRINT",EDGE,{"derivedFrom":sQuery(id+"F12.wireOp",EDGE,"E10.2.0.0")}),1.0]])]});
            var Q3;
            Q3=makeQuery(id+"F12.imprint","IMPRINT",FACE,{"disambiguationData":[TD([[makeQuery(id+"F12.imprint","IMPRINT",EDGE,{"derivedFrom":sQuery(id+"F12.wireOp",EDGE,"E10.3.0.0")}),1.0]])]});
            var Q4;
            Q4=makeQuery(id+"F12.imprint","IMPRINT",FACE,{"disambiguationData":[TD([[makeQuery(id+"F12.imprint","IMPRINT",EDGE,{"derivedFrom":sQuery(id+"F12.wireOp",EDGE,"E10.4.0.0")}),1.0]])]});
            var Q5;
            Q5=makeQuery(id+"F12.imprint","IMPRINT",FACE,{"disambiguationData":[TD([[makeQuery(id+"F12.imprint","IMPRINT",EDGE,{"derivedFrom":sQuery(id+"F12.wireOp",EDGE,"E10.5.0.0")}),1.0]])]});
            extrude(context, id + "F13", {"entities" : qUnion([Q0, Q1, Q2, Q3, Q4, Q5]), "operationType" : NewBodyOperationType.REMOVE, "oppositeDirection" : true, "depth" : 25.4 * mm});
        }
        {
            var Q0;
            Q0=makeQuery(id+"F1.opExtrude","CAP_FACE",FACE,{"disambiguationData":[OSD([sQuery(id+"F0.wireOp",EDGE,"E0.bottom"),sQuery(id+"F0.wireOp",EDGE,"E0.top"),sQuery(id+"F0.wireOp",EDGE,"E0.left"),sQuery(id+"F0.wireOp",EDGE,"E0.right")])],"isStart":false});
            var sketch = newSketch(context, id + "F14", { "sketchPlane" : qUnion([Q0])});
            skLineSegment(sketch, "E11.bottom", {"start": v(-756.92, 312.42) * mm, "end": v(756.92, 312.42) * mm});
            skLineSegment(sketch, "E11.top", {"start": v(-756.92, -312.42) * mm, "end": v(756.92, -312.42) * mm});
            skLineSegment(sketch, "E11.left", {"start": v(-756.92, 312.42) * mm, "end": v(-756.92, -312.42) * mm});
            skLineSegment(sketch, "E11.right", {"start": v(756.92, 312.42) * mm, "end": v(756.92, -312.42) * mm});
            skSolve(sketch);
        }
        {
            var Q0;
            Q0 = qSketchRegion(id + "F14", true);
            extrude(context, id + "F15", {"entities" : qUnion([Q0]), "operationType" : NewBodyOperationType.ADD, "depth" : 6.35 * mm});
        }
    });
